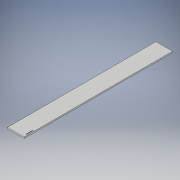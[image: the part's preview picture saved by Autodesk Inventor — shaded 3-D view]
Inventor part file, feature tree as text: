
AUTODESK INVENTOR PART (.ipt)
format: ipt  version: 2019.4 (Build 234330000, 330)  size: 194,048 bytes
history: native  units: in
note: dims shown in document units (in); Inventor stores cm internally (conversion verified against a paired STEP export)
features: extrude x2, sketch x2
ambient origin geometry x8: Origin, YZ Plane, XZ Plane, XY Plane, X Axis, Y Axis, Z Axis, Center Point
bodies: Solid1 (feature_tree)
feature tree (4):
  extrude  "Extrusion1"  Depth=1.752in
  extrude  "Extrusion2"  Depth=0.0028in
  sketch  "Sketch1"  dims[d0=0.1969in d1=1.752in]
  sketch  "Sketch2"  dims[d2=0.0157in d3=0.0in d4=0.0028in d5=0.0051in d6=0.0394in d7=0.0118in d8=7.874in d10=0.0039in d11=0.3937in d13=0.3937in d15=0.0012in d16=0.0in]
